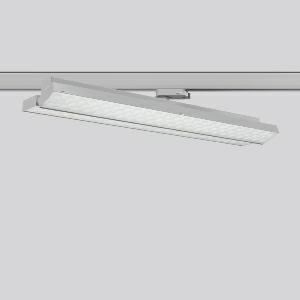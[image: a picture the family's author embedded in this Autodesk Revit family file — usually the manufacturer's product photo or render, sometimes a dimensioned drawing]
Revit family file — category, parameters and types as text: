
# Revit family: tx-move_742163_004_3_3268
name_source: partatom
category: Lighting Fixtures
units: mm (PartAtom-declared; Revit-internal decimal feet)

## family parameters
Cut with Voids When Loaded = No
Host = Face
Light Source = No
Part Type = Normal
Room Calculation Point = No
Round Connector Dimension = Use Diameter
Shared = No

## types (1)
- MultiLumen 1 (1 x LED Modul 835, 2875 lm, 3500)
    Apparent Load = 41 VA
    CIE Flux Codes = 65 90 98 100 100
    Color Rendering = 80
    Color Temperature = 3500
    Default Elevation = 1800 mm
    Description = Series: TX-MOVE
Multifunctional surface-mounted spotlight for area lighting. Very flat design. Housing: sheet steel, powder-coated. Rotation range: 356°. Swivel range: 90°. Consistent alignment possible with visible tilt scale. High-efficiency LED units with optimum light control thanks to clear plastic (PC) lens optics. Spezielle Mikrostrukturen reduzieren Gelbsaum. Asymmetrical light distribution. With multi adaptor for 3-circuit tracks 230 V. Suitable for Track on ceiling. MultiLumen: Luminous flux adjustable in 3 steps. Factory setting is the highest luminous flux. Environmentally friendly and resource-saving due to replaceable and recyclable components. 
Colour: silver, matt (approx. RAL 9006)
Length: 570 mm
Width: 119 mm
Height: 92 mm
Lamp: LED
Socket: without socket
Colour temperature: 3500K
Colour rendering index (CRI): 80
System power: 41 W
Rated luminous flux: 5750 lm
Luminous efficiency: 140 lm/W
System power 2: 57 W
Rated luminous flux 2: 7750 lm
Luminous efficiency 2: 136 lm/W
System power 3: 73 W
Rated luminous flux 3: 9450 lm
Luminous efficiency 3: 129 lm/W
Control gear: Regulated power supply
Protection class: I
Type of protection: IP 20
    Height = 75 mm
    Lamp = 1 x LED Modul 835
    Lamp Light Flux = 2875 lm
    Lamp count = 1
    Length = 569 mm
    Lifetime = 50000 h
    Luminous efficacy = 140 lm/W
    Manufacturer = RZB
    ModVariant = No
    Model = 742163.004.3
    Mounting Place = Ceiling
    Mounting Type = Rail mounted
    Number of Poles = 1
    OnlyDefault = Yes
    Power Factor = 1
    Product Name = TX-MOVE
    Product group = Track mounted projectors
    ProductGroupID = 301
    Protection Class = Protection class I
    Protection Degree = IP 20
    RLX_Detail_Level = 1
    RLX_Emergency_Light_Flux = 0 lm
    RLX_Emergency_Type = 0
    RLX_Emergency_Type_DB = No
    RlxData = <blob elided: 53941 chars, md5=8c4875df>
    Socket = socket
    Standby Power = 0 W
    System Light Flux = 5750 lm
    System Power = 41 W
    Type Comments = MultiLumen 1
    Type Image = 742162.004.jpg
    URL = http://relux.com
    VarID = multilumen_1
    Voltage = 230 V
    Voltage Range = 220-240 V
    Weight = 0.00 kg
    Width = 119 mm

## geometry (parser evidence)
native form markers: Blend x4, Sweep x16
no freeform markers — native parametric forms only
